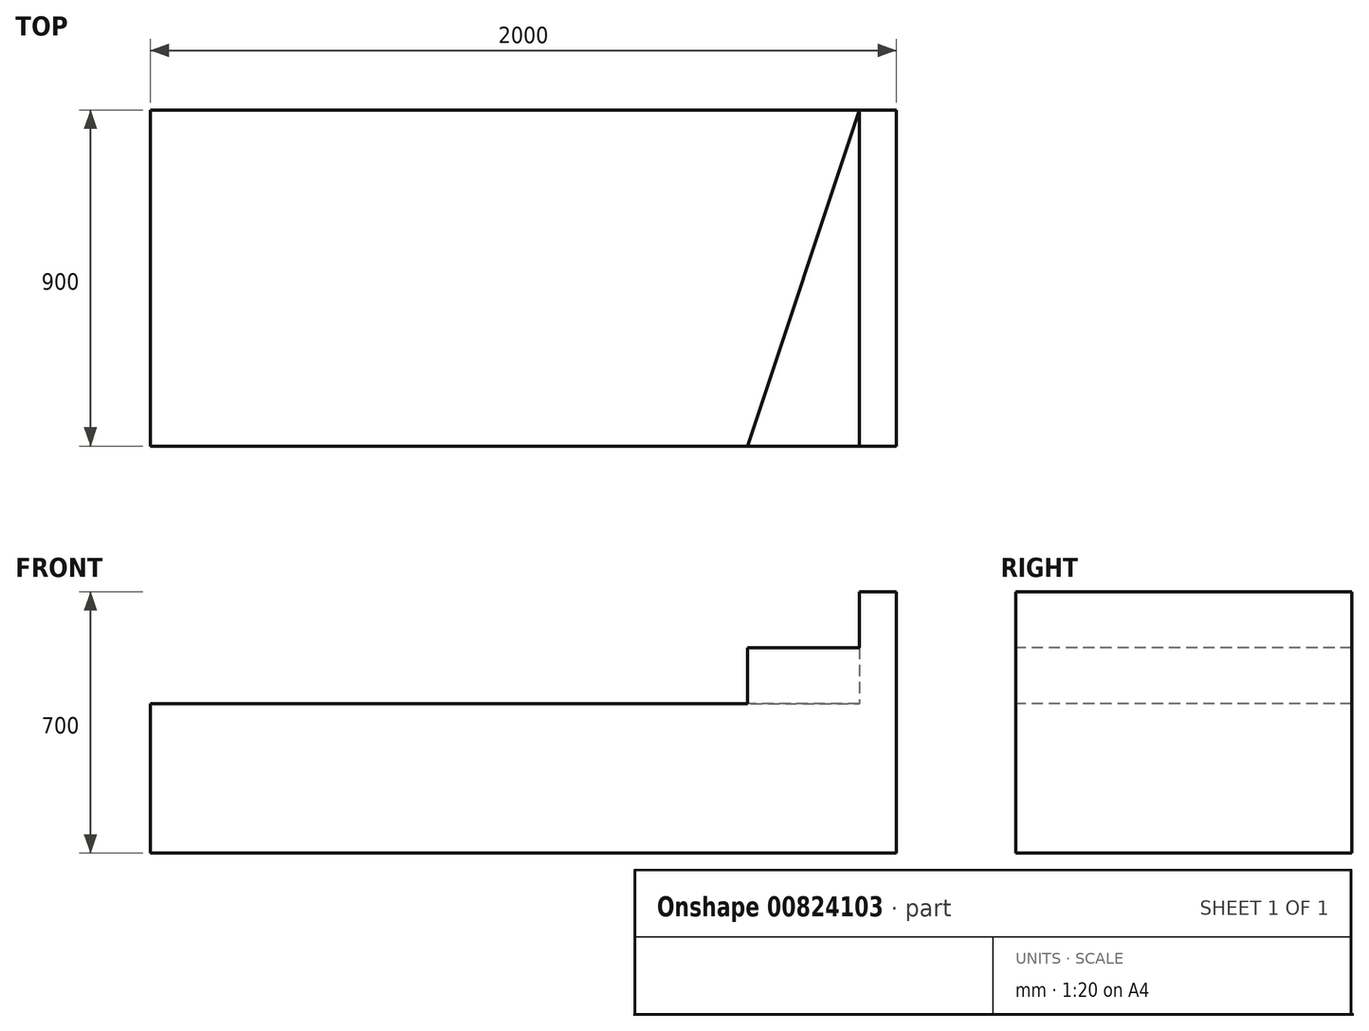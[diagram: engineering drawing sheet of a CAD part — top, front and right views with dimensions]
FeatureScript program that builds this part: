
annotation { "Feature Type Name" : "Feature", "Feature Type Description" : "" }
export const myFeature = defineFeature(function(context is Context, id is Id, definition is map)
    precondition{}
    {
        {
            var Q0;
            Q0=qCreatedBy(makeId("Top.planeOp"),FACE);
            var sketch = newSketch(context, id + "F0", { "sketchPlane" : qUnion([Q0])});
            skLineSegment(sketch, "E0.bottom", {"start": v(-1653.54, 0) * mm, "end": v(4346.46, 0) * mm});
            skLineSegment(sketch, "E0.top", {"start": v(-1653.54, -4000) * mm, "end": v(4346.46, -4000) * mm});
            skLineSegment(sketch, "E0.left", {"start": v(-1653.54, 0) * mm, "end": v(-1653.54, -4000) * mm});
            skLineSegment(sketch, "E0.right", {"start": v(4346.46, 0) * mm, "end": v(4346.46, -4000) * mm});
            skLineSegment(sketch, "E1", {"start": v(-1651.85, -1606.94) * mm, "end": v(-1251.85, -1606.94) * mm});
            skLineSegment(sketch, "E2", {"start": v(-1251.85, -1606.94) * mm, "end": v(-1251.85, -606.94) * mm});
            skLineSegment(sketch, "E3", {"start": v(-1251.85, -606.94) * mm, "end": v(148.15, -606.94) * mm});
            skLineSegment(sketch, "E4", {"start": v(148.15, -606.94) * mm, "end": v(148.15, -6.94) * mm});
            skLineSegment(sketch, "E5", {"start": v(148.15, -6.94) * mm, "end": v(-1651.85, -6.94) * mm});
            skLineSegment(sketch, "E6", {"start": v(-1651.85, -6.94) * mm, "end": v(-1651.85, -1606.94) * mm});
            skLineSegment(sketch, "E7", {"start": v(969.02, -358.32) * mm, "end": v(969.02, -1258.32) * mm});
            skLineSegment(sketch, "E8", {"start": v(969.02, -1258.32) * mm, "end": v(2569.02, -1258.32) * mm});
            skLineSegment(sketch, "E9", {"start": v(969.02, -358.32) * mm, "end": v(2869.02, -358.32) * mm});
            skLineSegment(sketch, "E10", {"start": v(2869.02, -358.32) * mm, "end": v(2569.02, -1258.32) * mm});
            skLineSegment(sketch, "E11", {"start": v(2869.02, -358.32) * mm, "end": v(2869.02, -1258.32) * mm});
            skLineSegment(sketch, "E12", {"start": v(2569.02, -1258.32) * mm, "end": v(2869.02, -1258.32) * mm});
            skLineSegment(sketch, "E13", {"start": v(2869.02, -358.32) * mm, "end": v(2969.02, -358.32) * mm});
            skLineSegment(sketch, "E14", {"start": v(2869.02, -1258.32) * mm, "end": v(2969.02, -1258.32) * mm});
            skLineSegment(sketch, "E15", {"start": v(2969.02, -358.32) * mm, "end": v(2969.02, -1258.32) * mm});
            skSolve(sketch);
        }
        {
            var Q0;
            Q0=makeQuery(id+"F0.imprint","IMPRINT",FACE,{"disambiguationData":[TD([[makeQuery(id+"F0.imprint","IMPRINT",EDGE,{"derivedFrom":sQuery(id+"F0.wireOp",EDGE,"E1")}),1.0]])]});
            var Q1;
            Q1=sQuery(id+"F0.wireOp",EDGE,"E3");
            var Q2;
            Q2=sQuery(id+"F0.wireOp",EDGE,"E4");
            var Q3;
            Q3=sQuery(id+"F0.wireOp",EDGE,"E5");
            var Q4;
            Q4=sQuery(id+"F0.wireOp",EDGE,"E7");
            extrude(context, id + "F1", {"entities" : qUnion([Q0]), "bodyType" : ToolBodyType.SURFACE, "surfaceEntities" : qUnion([Q1, Q2, Q3, Q4]), "depth" : 200 * mm, "offsetDistance" : 25 * mm});
        }
        {
            var Q0;
            Q0=makeQuery(id+"F0.imprint","IMPRINT",FACE,{"disambiguationData":[TD([[makeQuery(id+"F0.imprint","IMPRINT",EDGE,{"derivedFrom":sQuery(id+"F0.wireOp",EDGE,"E7")}),1.0]])]});
            extrude(context, id + "F2", {"entities" : qUnion([Q0]), "depth" : 400 * mm, "offsetDistance" : 25 * mm});
        }
        {
            var Q0;
            Q0=makeQuery(id+"F0.imprint","IMPRINT",FACE,{"disambiguationData":[TD([[makeQuery(id+"F0.imprint","IMPRINT",EDGE,{"derivedFrom":sQuery(id+"F0.wireOp",EDGE,"E10")}),1.0]])]});
            extrude(context, id + "F3", {"entities" : qUnion([Q0]), "operationType" : NewBodyOperationType.ADD, "depth" : 550 * mm, "offsetDistance" : 25 * mm});
        }
        {
            var Q0;
            Q0=makeQuery(id+"F0.imprint","IMPRINT",FACE,{"disambiguationData":[TD([[makeQuery(id+"F0.imprint","IMPRINT",EDGE,{"derivedFrom":sQuery(id+"F0.wireOp",EDGE,"E11")}),1.0]])]});
            extrude(context, id + "F4", {"entities" : qUnion([Q0]), "operationType" : NewBodyOperationType.ADD, "depth" : 700 * mm, "offsetDistance" : 25 * mm});
        }
    });
